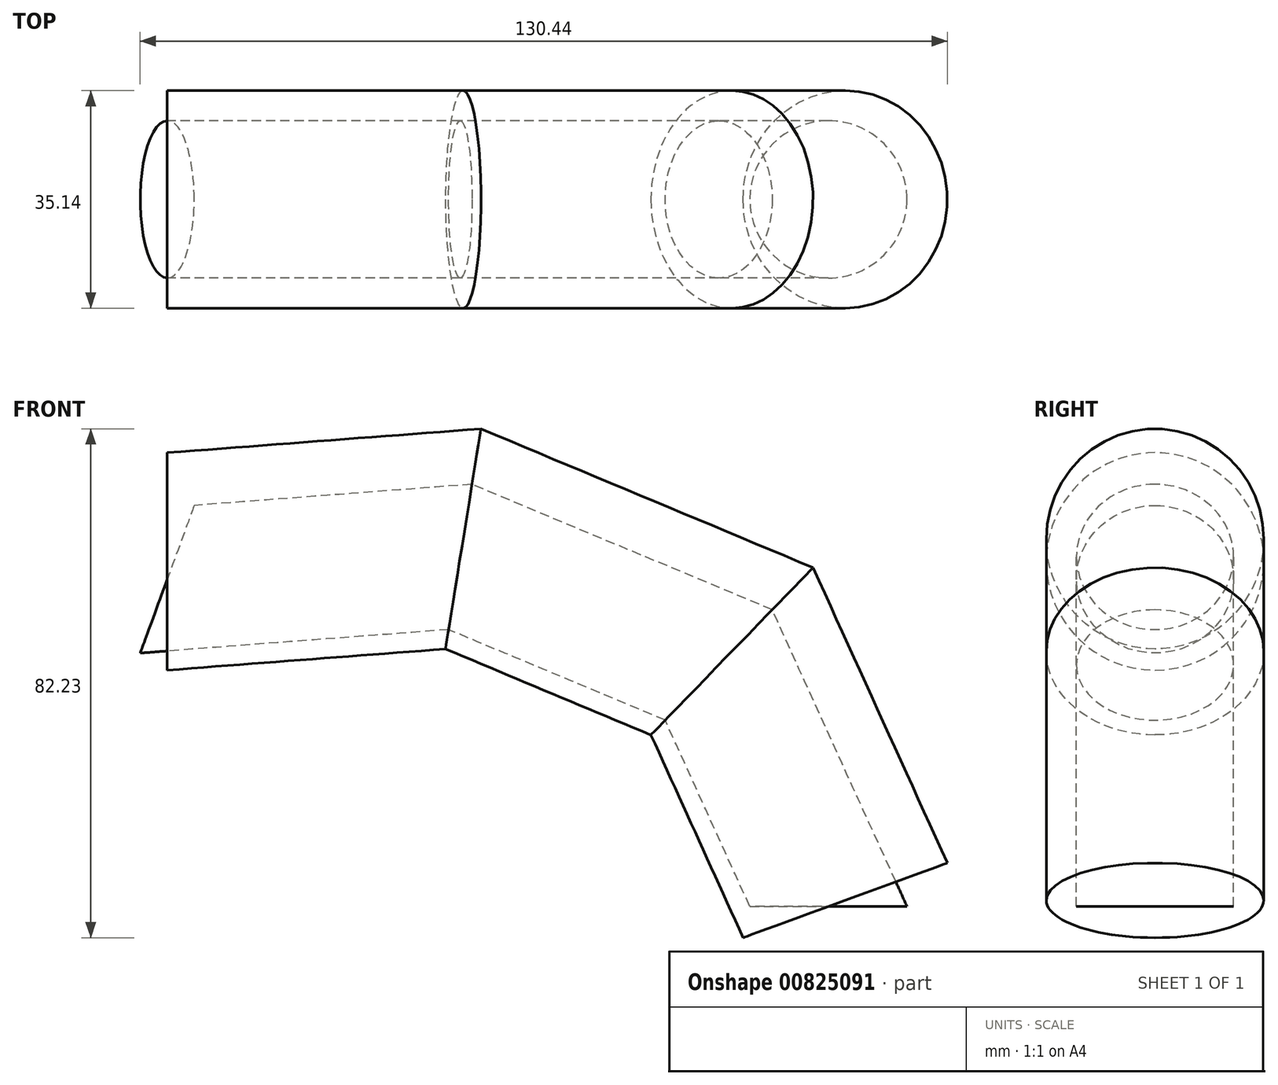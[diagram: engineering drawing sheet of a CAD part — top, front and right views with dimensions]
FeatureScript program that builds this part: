
annotation { "Feature Type Name" : "Feature", "Feature Type Description" : "" }
export const myFeature = defineFeature(function(context is Context, id is Id, definition is map)
    precondition{}
    {
        {
            var Q0;
            Q0=qCreatedBy(makeId("Top.planeOp"),FACE);
            var sketch = newSketch(context, id + "F0", { "sketchPlane" : qUnion([Q0])});
            skCircle(sketch, "E0", {"center": v(0, 0) * mm, "radius": 12.7 * mm});
            skSolve(sketch);
        }
        {
            var Q0;
            Q0=qCreatedBy(makeId("Right.planeOp"),FACE);
            cPlane(context, id + "F1", {"entities" : qUnion([Q0]), "cplaneType" : CPlaneType.OFFSET, "offset" : 101.6 * mm, "oppositeDirection" : true, "width" : 152.4 * mm, "height" : 152.4 * mm});
        }
        {
            var Q0;
            Q0=qCreatedBy(id+"F1.planeOp",FACE);
            var sketch = newSketch(context, id + "F2", { "sketchPlane" : qUnion([Q0])});
            skCircle(sketch, "E1", {"center": v(0, 56.15) * mm, "radius": 17.57 * mm});
            skSolve(sketch);
        }
        {
            var Q0;
            Q0=qCreatedBy(makeId("Front.planeOp"),FACE);
            var sketch = newSketch(context, id + "F3", { "sketchPlane" : qUnion([Q0])});
            skLineSegment(sketch, "E2", {"start": v(0, 0) * mm, "end": v(-17.74, 39.02) * mm});
            skLineSegment(sketch, "E3", {"start": v(-17.74, 39.02) * mm, "end": v(-59.5, 56.47) * mm});
            skLineSegment(sketch, "E4", {"start": v(-59.5, 56.47) * mm, "end": v(-106.86, 52.87) * mm});
            skSolve(sketch);
        }
        {
            var Q0;
            Q0=makeQuery(id+"F2.imprint","IMPRINT",FACE,{"disambiguationData":[TD([[makeQuery(id+"F2.imprint","IMPRINT",EDGE,{"derivedFrom":sQuery(id+"F2.wireOp",EDGE,"E1")}),1.0]])]});
            var Q1;
            Q1=makeQuery(id+"F0.imprint","IMPRINT",FACE,{"disambiguationData":[TD([[makeQuery(id+"F0.imprint","IMPRINT",EDGE,{"derivedFrom":sQuery(id+"F0.wireOp",EDGE,"E0")}),1.0]])]});
            var Q2;
            Q2=sQuery(id+"F3.wireOp",EDGE,"E4");
            var Q3;
            Q3=sQuery(id+"F3.wireOp",EDGE,"E3");
            var Q4;
            Q4=sQuery(id+"F3.wireOp",EDGE,"E2");
            sweep(context, id + "F4", {"profiles" : qUnion([Q0, Q1]), "path" : qUnion([Q2, Q3, Q4])});
        }
    });
